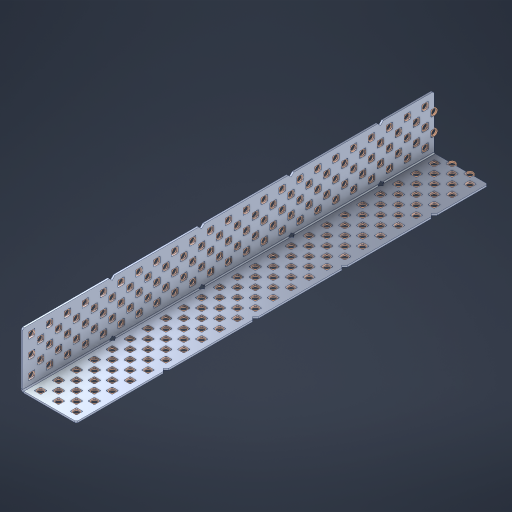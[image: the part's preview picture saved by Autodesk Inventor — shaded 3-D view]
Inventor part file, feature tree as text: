
AUTODESK INVENTOR PART (.ipt)
format: ipt  version: 2023 (Build 270158000, 158)  size: 2,421,248 bytes
history: native  units: in
note: dims shown in document units (in); Inventor stores cm internally (conversion verified against a paired STEP export)
features: other x236, extrude x228, sheet_metal_op x8, sketch x7, pattern_linear x3, mirror x1, chamfer x1
ambient origin geometry x8: Origin, YZ Plane, XZ Plane, XY Plane, X Axis, Y Axis, Z Axis, Center Point
bodies: Solid1 (feature_tree), Body (feature_tree)
feature tree (484):
  sheet_metal_op  "Flanges"
  sheet_metal_op  "Body Pattern"
  pattern_linear  "Center Double"  Spacing1=1.5in  [1 undecoded]
  pattern_linear  "Center Pattern"  Spacing1=0.1875in  [1 undecoded]
  other  "Arc Length"
  pattern_linear  "Notch Pattern"  Spacing1=0.0469in  [1 undecoded]
  other  "Diagonal Plane"
  mirror  "Everything Mirrored"
  chamfer  "End Chamfer"
  sketch  "Sketch1"  dims[d0=1.5in]
  other  "Plate1"
  sketch  "Sketch2"  dims[d1=11.5in]
  other  "Plate2"
  sheet_metal_op  "Bend1"
  sheet_metal_op  "Corner1"
  sketch  "Sketch8"  dims[d2=0.0469in]
  sketch  "Sketch9"  dims[d3=0.0469in]
  other  "Srf91"
  sheet_metal_op  "Body Pattern Sketch"
  other  "Srf92"
  sketch  "Sketch13"  dims[d4=0.0234in]
  sketch  "Sketch15"  dims[d5=0.0938in]
  sketch  "Sketch16"  dims[d6=0.0469in d7=1.5in d8=90.0deg d9=0.0312in d10=0.1875in d11=0.0469in d12=0.0469in d49=0.182in d50=0.02in d52=0.25in d53=0.0469in d54=0.0in d55=0.172in d56=1.0in d57=0.0in d85=0.1473in d86=0.1659in d89=0.0469in d90=0.0in d91=0.04in d92=0.0491in d95=2.5in d96=0.04in d97=0.25in d98=45.0deg d106=0.182in d107=0.02in d110=0.0469in d111=0.0in d112=0.172in d113=0.5in d114=0.0in d117=0.5in d126=0.0491in d127=0.1227in d128=0.08in d129=0.04in d130=2.5in d131=0.25in d132=9.0551in d134=0.5in d135=1.1811in d137=0.5in d140=0.5in d141=1.0in d142=0.3937in d144=0.5in d145=0.071in d146=0.7874in d148=0.5in]
  other  "Srf786"
  other  "Srf856"
  other  "Srf889"
  other  "Srf890"
  other  "Srf891"
  other  "Srf1275"
  other  "Srf1276"
  other  "Srf1278"
  other  "Srf1277"
  other  "Srf1285"
  other  "Srf1286"
  other  "Srf1287"
  other  "Srf1445"
  other  "Srf1446"
  other  "Srf1447"
  other  "Srf1448"
  other  "Srf1449"
  other  "Srf1537"
  other  "Srf1538"
  other  "Srf1539"
  other  "Srf1540"
  other  "Srf1541"
  other  "Srf1807"
  other  "Srf1808"
  other  "Srf1809"
  other  "Srf1810"
  other  "Srf1811"
  other  "Srf1812"
  other  "Srf1813"
  other  "Srf1814"
  other  "Srf1815"
  other  "Srf1816"
  other  "Srf1817"
  other  "Srf1818"
  other  "Srf1819"
  other  "Srf1820"
  other  "Srf1959"
  other  "Srf1960"
  other  "Srf1961"
  other  "Srf1962"
  other  "Srf1963"
  other  "Srf1964"
  other  "Srf1965"
  other  "Srf1966"
  other  "Srf1967"
  other  "Srf1968"
  other  "Srf1969"
  other  "Srf1970"
  other  "Srf1971"
  other  "Srf1972"
  other  "Srf2009"
  other  "Srf2010"
  other  "Srf2011"
  other  "Srf2012"
  other  "Srf2013"
  other  "Srf2014"
  other  "Srf2015"
  other  "Srf2016"
  other  "Srf2017"
  other  "Srf2018"
  other  "Srf2019"
  other  "Srf2020"
  other  "Srf2021"
  other  "Srf2022"
  other  "Srf2023"
  other  "Srf2024"
  other  "Srf2025"
  other  "Srf2026"
  other  "Srf2027"
  other  "Srf2028"
  other  "Srf2029"
  other  "Srf2030"
  other  "Srf2031"
  other  "Srf2043"
  other  "Srf2044"
  other  "Srf2045"
  other  "Srf2046"
  other  "Srf2047"
  other  "Srf2048"
  other  "Srf2049"
  other  "Srf2050"
  other  "Srf2051"
  other  "Srf2052"
  other  "Srf2053"
  other  "Srf2054"
  other  "Srf2055"
  other  "Srf2056"
  other  "Srf2057"
  other  "Srf2058"
  other  "Srf2059"
  other  "Srf2060"
  other  "Srf2061"
  other  "Srf2062"
  other  "Srf2063"
  other  "Srf2064"
  other  "Srf2076"
  other  "Srf2077"
  other  "Srf2078"
  other  "Srf2079"
  other  "Srf2080"
  other  "Srf2081"
  other  "Srf2082"
  other  "Srf2083"
  other  "Srf2084"
  other  "Srf2085"
  other  "Srf2086"
  other  "Srf2087"
  other  "Srf2088"
  other  "Srf2089"
  other  "Srf2090"
  other  "Srf2091"
  other  "Srf2092"
  other  "Srf2093"
  other  "Srf2094"
  other  "Srf2095"
  other  "Srf2096"
  other  "Srf2097"
  other  "Srf2098"
  other  "Srf2099"
  other  "Srf2100"
  other  "Srf2101"
  other  "Srf2102"
  other  "Srf2103"
  other  "Srf2104"
  other  "Srf2105"
  other  "Srf2106"
  other  "Srf2107"
  other  "Srf2108"
  other  "Srf2109"
  other  "Srf2110"
  other  "Srf2111"
  other  "Srf2112"
  other  "Srf2113"
  other  "Srf2114"
  other  "Srf2115"
  other  "Srf2116"
  other  "Srf2117"
  other  "Srf2118"
  other  "Srf2119"
  other  "Srf2120"
  other  "Srf2121"
  other  "Srf2122"
  other  "Srf2123"
  other  "Srf2124"
  other  "Srf2125"
  other  "Srf2126"
  other  "Srf2127"
  other  "Srf2128"
  other  "Srf2129"
  other  "Srf2130"
  other  "Srf2131"
  other  "Srf2132"
  other  "Srf2133"
  other  "Srf2134"
  other  "Srf2135"
  other  "Srf2136"
  other  "Srf2137"
  other  "Srf2138"
  other  "Srf2139"
  other  "Srf2140"
  other  "Srf2141"
  other  "Srf2142"
  other  "Srf2179"
  other  "Srf2180"
  other  "Srf2181"
  other  "Srf2182"
  other  "Srf2183"
  other  "Srf2184"
  other  "Srf2185"
  other  "Srf2186"
  other  "Srf2187"
  other  "Srf2188"
  other  "Srf2189"
  other  "Srf2190"
  other  "Srf2191"
  other  "Srf2192"
  other  "Srf2193"
  other  "Srf2194"
  other  "Srf2195"
  other  "Srf2196"
  other  "Srf2197"
  other  "Srf2198"
  other  "Srf2199"
  other  "Srf2200"
  other  "Srf2201"
  other  "Srf2202"
  other  "Srf2203"
  other  "Srf2204"
  other  "Srf2205"
  other  "Srf2206"
  other  "Srf2207"
  other  "Srf2208"
  other  "Srf2209"
  other  "Srf2210"
  other  "Srf2211"
  other  "Srf2212"
  other  "Srf2213"
  other  "Srf2214"
  other  "Srf2215"
  other  "Srf2216"
  other  "Srf2217"
  other  "Srf2218"
  other  "Srf2219"
  other  "Srf2220"
  other  "Srf2221"
  other  "Srf2222"
  other  "Srf2223"
  other  "Srf2224"
  other  "Srf2225"
  other  "Srf2226"
  other  "Srf2227"
  other  "Srf2228"
  other  "Srf2229"
  other  "Srf2230"
  other  "Srf2231"
  other  "Srf2232"
  other  "Srf2233"
  other  "Srf2234"
  other  "Srf2235"
  other  "Srf2236"
  other  "Srf2237"
  other  "Srf2238"
  other  "Srf2239"
  other  "Srf2240"
  other  "Srf2241"
  other  "Srf2242"
  other  "Srf2243"
  other  "Srf2244"
  sheet_metal_op  "Body Stamp"
  sheet_metal_op  "Body Circle"
  other  "Center Stamp"
  other  "Center Circle"
  sheet_metal_op  "Notch"
  extrude  "ExtrusionSrf92"  Depth=0.0469in
  extrude  "ExtrusionSrf856"  Depth=0.182in
  extrude  "ExtrusionSrf889"  Depth=0.02in
  extrude  "ExtrusionSrf890"  Depth=0.25in
  extrude  "ExtrusionSrf891"  Depth=0.0469in
  extrude  "ExtrusionSrf1275"  TaperAngle=0.0deg  [1 undecoded]
  extrude  "ExtrusionSrf1276"  Depth=0.5in
  extrude  "ExtrusionSrf1277"  Depth=1.0in TaperAngle=0.0deg
  extrude  "ExtrusionSrf1345"  Depth=0.5in
  extrude  "ExtrusionSrf1346"  Depth=0.5in
  extrude  "ExtrusionSrf1347"  Depth=0.0469in
  extrude  "ExtrusionSrf1348"  Depth=0.5in TaperAngle=0.0deg
  extrude  "ExtrusionSrf1445"  Depth=0.5in
  extrude  "ExtrusionSrf1446"  Depth=0.25in TaperAngle=45.0deg
  extrude  "ExtrusionSrf1447"  Depth=0.182in
  extrude  "ExtrusionSrf1448"  Depth=0.02in
  extrude  "ExtrusionSrf1449"  Depth=0.0469in
  extrude  "ExtrusionSrf1537"  TaperAngle=0.0deg  [1 undecoded]
  extrude  "ExtrusionSrf1538"  Depth=0.5in
  extrude  "ExtrusionSrf1539"  Depth=0.5in TaperAngle=0.0deg
  extrude  "ExtrusionSrf1540"  Depth=0.5in
  extrude  "ExtrusionSrf1541"  Depth=0.5in
  extrude  "ExtrusionSrf1807"  Depth=0.5in
  extrude  "ExtrusionSrf1808"  Depth=0.5in
  extrude  "ExtrusionSrf1809"  Depth=0.5in
  extrude  "ExtrusionSrf1810"  Depth=0.5in
  extrude  "ExtrusionSrf1811"  Depth=0.25in
  extrude  "ExtrusionSrf1812"  Depth=0.5in
  extrude  "ExtrusionSrf1813"  Depth=0.5in
  extrude  "ExtrusionSrf1814"  Depth=0.5in
  extrude  "ExtrusionSrf1815"  Depth=1.0in
  extrude  "ExtrusionSrf1816"  Depth=0.3937in
  extrude  "ExtrusionSrf1817"  Depth=0.5in
  extrude  "ExtrusionSrf1818"  Depth=0.5in
  extrude  "ExtrusionSrf1819"  [1 undecoded]
  extrude  "ExtrusionSrf1820"  [1 undecoded]
  extrude  "ExtrusionSrf1959"  [1 undecoded]
  extrude  "ExtrusionSrf1960"  [1 undecoded]
  extrude  "ExtrusionSrf1961"  [1 undecoded]
  extrude  "ExtrusionSrf1962"  [1 undecoded]
  extrude  "ExtrusionSrf1963"  [1 undecoded]
  extrude  "ExtrusionSrf1964"  [1 undecoded]
  extrude  "ExtrusionSrf1965"  [1 undecoded]
  extrude  "ExtrusionSrf1966"  [1 undecoded]
  extrude  "ExtrusionSrf1967"  [1 undecoded]
  extrude  "ExtrusionSrf1968"  [1 undecoded]
  extrude  "ExtrusionSrf1969"  [1 undecoded]
  extrude  "ExtrusionSrf1970"  [1 undecoded]
  extrude  "ExtrusionSrf1971"  [1 undecoded]
  extrude  "ExtrusionSrf1972"  [1 undecoded]
  extrude  "ExtrusionSrf2009"  [1 undecoded]
  extrude  "ExtrusionSrf2010"  [1 undecoded]
  extrude  "ExtrusionSrf2011"  [1 undecoded]
  extrude  "ExtrusionSrf2012"  [1 undecoded]
  extrude  "ExtrusionSrf2013"  [1 undecoded]
  extrude  "ExtrusionSrf2014"  [1 undecoded]
  extrude  "ExtrusionSrf2015"  [1 undecoded]
  extrude  "ExtrusionSrf2016"  [1 undecoded]
  extrude  "ExtrusionSrf2017"  [1 undecoded]
  extrude  "ExtrusionSrf2018"  [1 undecoded]
  extrude  "ExtrusionSrf2019"  [1 undecoded]
  extrude  "ExtrusionSrf2020"  [1 undecoded]
  extrude  "ExtrusionSrf2021"  [1 undecoded]
  extrude  "ExtrusionSrf2022"  [1 undecoded]
  extrude  "ExtrusionSrf2023"  [1 undecoded]
  extrude  "ExtrusionSrf2024"  [1 undecoded]
  extrude  "ExtrusionSrf2025"  [1 undecoded]
  extrude  "ExtrusionSrf2026"  [1 undecoded]
  extrude  "ExtrusionSrf2027"  [1 undecoded]
  extrude  "ExtrusionSrf2028"  [1 undecoded]
  extrude  "ExtrusionSrf2029"  [1 undecoded]
  extrude  "ExtrusionSrf2030"  [1 undecoded]
  extrude  "ExtrusionSrf2031"  [1 undecoded]
  extrude  "ExtrusionSrf2043"  [1 undecoded]
  extrude  "ExtrusionSrf2044"  [1 undecoded]
  extrude  "ExtrusionSrf2045"  [1 undecoded]
  extrude  "ExtrusionSrf2046"  [1 undecoded]
  extrude  "ExtrusionSrf2047"  [1 undecoded]
  extrude  "ExtrusionSrf2048"  [1 undecoded]
  extrude  "ExtrusionSrf2049"  [1 undecoded]
  extrude  "ExtrusionSrf2050"  [1 undecoded]
  extrude  "ExtrusionSrf2051"  [1 undecoded]
  extrude  "ExtrusionSrf2052"  [1 undecoded]
  extrude  "ExtrusionSrf2053"  [1 undecoded]
  extrude  "ExtrusionSrf2054"  [1 undecoded]
  extrude  "ExtrusionSrf2055"  [1 undecoded]
  extrude  "ExtrusionSrf2056"  [1 undecoded]
  extrude  "ExtrusionSrf2057"  [1 undecoded]
  extrude  "ExtrusionSrf2058"  [1 undecoded]
  extrude  "ExtrusionSrf2059"  [1 undecoded]
  extrude  "ExtrusionSrf2060"  [1 undecoded]
  extrude  "ExtrusionSrf2061"  [1 undecoded]
  extrude  "ExtrusionSrf2062"  [1 undecoded]
  extrude  "ExtrusionSrf2063"  [1 undecoded]
  extrude  "ExtrusionSrf2064"  [1 undecoded]
  extrude  "ExtrusionSrf2076"  [1 undecoded]
  extrude  "ExtrusionSrf2077"  [1 undecoded]
  extrude  "ExtrusionSrf2078"  [1 undecoded]
  extrude  "ExtrusionSrf2079"  [1 undecoded]
  extrude  "ExtrusionSrf2080"  [1 undecoded]
  extrude  "ExtrusionSrf2081"  [1 undecoded]
  extrude  "ExtrusionSrf2082"  [1 undecoded]
  extrude  "ExtrusionSrf2083"  [1 undecoded]
  extrude  "ExtrusionSrf2084"  [1 undecoded]
  extrude  "ExtrusionSrf2085"  [1 undecoded]
  extrude  "ExtrusionSrf2086"  [1 undecoded]
  extrude  "ExtrusionSrf2087"  [1 undecoded]
  extrude  "ExtrusionSrf2088"  [1 undecoded]
  extrude  "ExtrusionSrf2089"  [1 undecoded]
  extrude  "ExtrusionSrf2090"  [1 undecoded]
  extrude  "ExtrusionSrf2091"  [1 undecoded]
  extrude  "ExtrusionSrf2092"  [1 undecoded]
  extrude  "ExtrusionSrf2093"  [1 undecoded]
  extrude  "ExtrusionSrf2094"  [1 undecoded]
  extrude  "ExtrusionSrf2095"  [1 undecoded]
  extrude  "ExtrusionSrf2096"  [1 undecoded]
  extrude  "ExtrusionSrf2097"  [1 undecoded]
  extrude  "ExtrusionSrf2098"  [1 undecoded]
  extrude  "ExtrusionSrf2099"  [1 undecoded]
  extrude  "ExtrusionSrf2100"  [1 undecoded]
  extrude  "ExtrusionSrf2101"  [1 undecoded]
  extrude  "ExtrusionSrf2102"  [1 undecoded]
  extrude  "ExtrusionSrf2103"  [1 undecoded]
  extrude  "ExtrusionSrf2104"  [1 undecoded]
  extrude  "ExtrusionSrf2105"  [1 undecoded]
  extrude  "ExtrusionSrf2106"  [1 undecoded]
  extrude  "ExtrusionSrf2107"  [1 undecoded]
  extrude  "ExtrusionSrf2108"  [1 undecoded]
  extrude  "ExtrusionSrf2109"  [1 undecoded]
  extrude  "ExtrusionSrf2110"  [1 undecoded]
  extrude  "ExtrusionSrf2111"  [1 undecoded]
  extrude  "ExtrusionSrf2112"  [1 undecoded]
  extrude  "ExtrusionSrf2113"  [1 undecoded]
  extrude  "ExtrusionSrf2114"  [1 undecoded]
  extrude  "ExtrusionSrf2115"  [1 undecoded]
  extrude  "ExtrusionSrf2116"  [1 undecoded]
  extrude  "ExtrusionSrf2117"  [1 undecoded]
  extrude  "ExtrusionSrf2118"  [1 undecoded]
  extrude  "ExtrusionSrf2119"  [1 undecoded]
  extrude  "ExtrusionSrf2120"  [1 undecoded]
  extrude  "ExtrusionSrf2121"  [1 undecoded]
  extrude  "ExtrusionSrf2122"  [1 undecoded]
  extrude  "ExtrusionSrf2123"  [1 undecoded]
  extrude  "ExtrusionSrf2124"  [1 undecoded]
  extrude  "ExtrusionSrf2125"  [1 undecoded]
  extrude  "ExtrusionSrf2126"  [1 undecoded]
  extrude  "ExtrusionSrf2127"  [1 undecoded]
  extrude  "ExtrusionSrf2128"  [1 undecoded]
  extrude  "ExtrusionSrf2129"  [1 undecoded]
  extrude  "ExtrusionSrf2130"  [1 undecoded]
  extrude  "ExtrusionSrf2131"  [1 undecoded]
  extrude  "ExtrusionSrf2132"  [1 undecoded]
  extrude  "ExtrusionSrf2133"  [1 undecoded]
  extrude  "ExtrusionSrf2134"  [1 undecoded]
  extrude  "ExtrusionSrf2135"  [1 undecoded]
  extrude  "ExtrusionSrf2136"  [1 undecoded]
  extrude  "ExtrusionSrf2137"  [1 undecoded]
  extrude  "ExtrusionSrf2138"  [1 undecoded]
  extrude  "ExtrusionSrf2139"  [1 undecoded]
  extrude  "ExtrusionSrf2140"  [1 undecoded]
  extrude  "ExtrusionSrf2141"  [1 undecoded]
  extrude  "ExtrusionSrf2142"  [1 undecoded]
  extrude  "ExtrusionSrf2179"  [1 undecoded]
  extrude  "ExtrusionSrf2180"  [1 undecoded]
  extrude  "ExtrusionSrf2181"  [1 undecoded]
  extrude  "ExtrusionSrf2182"  [1 undecoded]
  extrude  "ExtrusionSrf2183"  [1 undecoded]
  extrude  "ExtrusionSrf2184"  [1 undecoded]
  extrude  "ExtrusionSrf2185"  [1 undecoded]
  extrude  "ExtrusionSrf2186"  [1 undecoded]
  extrude  "ExtrusionSrf2187"  [1 undecoded]
  extrude  "ExtrusionSrf2188"  [1 undecoded]
  extrude  "ExtrusionSrf2189"  [1 undecoded]
  extrude  "ExtrusionSrf2190"  [1 undecoded]
  extrude  "ExtrusionSrf2191"  [1 undecoded]
  extrude  "ExtrusionSrf2192"  [1 undecoded]
  extrude  "ExtrusionSrf2193"  [1 undecoded]
  extrude  "ExtrusionSrf2194"  [1 undecoded]
  extrude  "ExtrusionSrf2195"  [1 undecoded]
  extrude  "ExtrusionSrf2196"  [1 undecoded]
  extrude  "ExtrusionSrf2197"  [1 undecoded]
  extrude  "ExtrusionSrf2198"  [1 undecoded]
  extrude  "ExtrusionSrf2199"  [1 undecoded]
  extrude  "ExtrusionSrf2200"  [1 undecoded]
  extrude  "ExtrusionSrf2201"  [1 undecoded]
  extrude  "ExtrusionSrf2202"  [1 undecoded]
  extrude  "ExtrusionSrf2203"  [1 undecoded]
  extrude  "ExtrusionSrf2204"  [1 undecoded]
  extrude  "ExtrusionSrf2205"  [1 undecoded]
  extrude  "ExtrusionSrf2206"  [1 undecoded]
  extrude  "ExtrusionSrf2207"  [1 undecoded]
  extrude  "ExtrusionSrf2208"  [1 undecoded]
  extrude  "ExtrusionSrf2209"  [1 undecoded]
  extrude  "ExtrusionSrf2210"  [1 undecoded]
  extrude  "ExtrusionSrf2211"  [1 undecoded]
  extrude  "ExtrusionSrf2212"  [1 undecoded]
  extrude  "ExtrusionSrf2213"  [1 undecoded]
  extrude  "ExtrusionSrf2214"  [1 undecoded]
  extrude  "ExtrusionSrf2215"  [1 undecoded]
  extrude  "ExtrusionSrf2216"  [1 undecoded]
  extrude  "ExtrusionSrf2217"  [1 undecoded]
  extrude  "ExtrusionSrf2218"  [1 undecoded]
  extrude  "ExtrusionSrf2219"  [1 undecoded]
  extrude  "ExtrusionSrf2220"  [1 undecoded]
  extrude  "ExtrusionSrf2221"  [1 undecoded]
  extrude  "ExtrusionSrf2222"  [1 undecoded]
  extrude  "ExtrusionSrf2223"  [1 undecoded]
  extrude  "ExtrusionSrf2224"  [1 undecoded]
  extrude  "ExtrusionSrf2225"  [1 undecoded]
  extrude  "ExtrusionSrf2226"  [1 undecoded]
  extrude  "ExtrusionSrf2227"  [1 undecoded]
  extrude  "ExtrusionSrf2228"  [1 undecoded]
  extrude  "ExtrusionSrf2229"  [1 undecoded]
  extrude  "ExtrusionSrf2230"  [1 undecoded]
  extrude  "ExtrusionSrf2231"  [1 undecoded]
  extrude  "ExtrusionSrf2232"  [1 undecoded]
  extrude  "ExtrusionSrf2233"  [1 undecoded]
  extrude  "ExtrusionSrf2234"  [1 undecoded]
  extrude  "ExtrusionSrf2235"  [1 undecoded]
  extrude  "ExtrusionSrf2236"  [1 undecoded]
  extrude  "ExtrusionSrf2237"  [1 undecoded]
  extrude  "ExtrusionSrf2238"  [1 undecoded]
  extrude  "ExtrusionSrf2239"  [1 undecoded]
  extrude  "ExtrusionSrf2240"  [1 undecoded]
  extrude  "ExtrusionSrf2241"  [1 undecoded]
  extrude  "ExtrusionSrf2242"  [1 undecoded]
  extrude  "ExtrusionSrf2243"  [1 undecoded]
  extrude  "ExtrusionSrf2244"  [1 undecoded]
note: 199 required parameter values undecoded (feature->parameter linkage not recoverable at this tier; creation-order binding heuristic only, values carry confidence <= 0.55)
